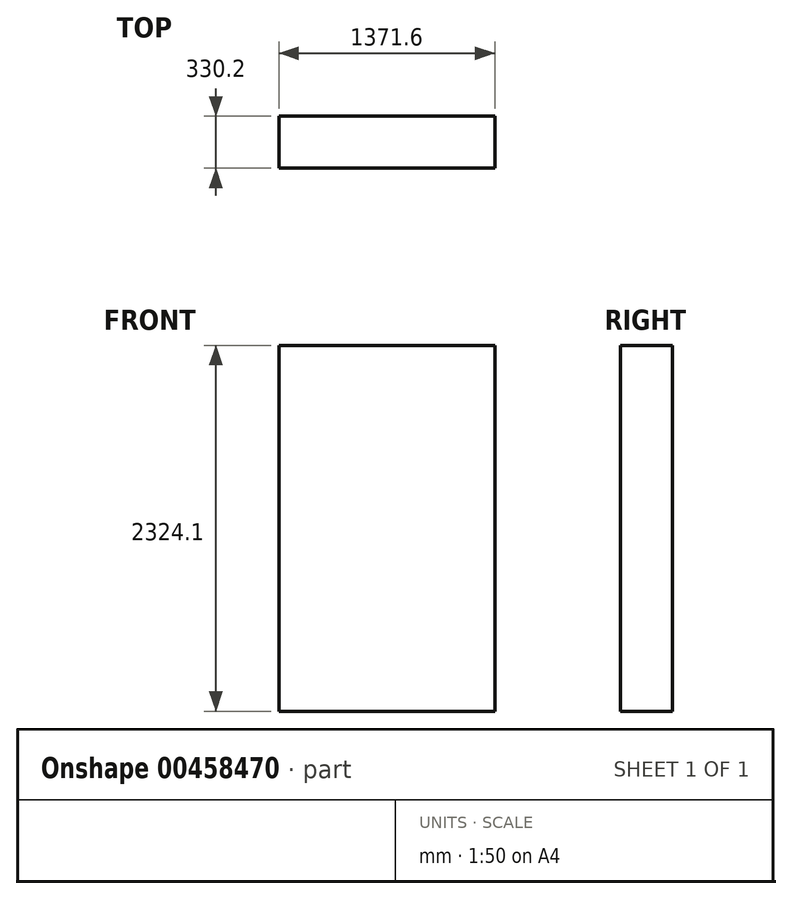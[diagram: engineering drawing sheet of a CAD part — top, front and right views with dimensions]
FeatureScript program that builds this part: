
annotation { "Feature Type Name" : "Feature", "Feature Type Description" : "" }
export const myFeature = defineFeature(function(context is Context, id is Id, definition is map)
    precondition{}
    {
        {
            var Q0;
            Q0=qCreatedBy(makeId("Top.planeOp"),FACE);
            var sketch = newSketch(context, id + "F0", { "sketchPlane" : qUnion([Q0])});
            skLineSegment(sketch, "E0.bottom", {"start": v(-660.33, 158.27) * mm, "end": v(711.27, 158.27) * mm});
            skLineSegment(sketch, "E0.top", {"start": v(-660.33, -171.93) * mm, "end": v(711.27, -171.93) * mm});
            skLineSegment(sketch, "E0.left", {"start": v(-660.33, 158.27) * mm, "end": v(-660.33, -171.93) * mm});
            skLineSegment(sketch, "E0.right", {"start": v(711.27, 158.27) * mm, "end": v(711.27, -171.93) * mm});
            skSolve(sketch);
        }
        {
            var Q0;
            Q0=sQuery(id+"F0.wireOp",EDGE,"E0.bottom");
            var Q1;
            Q1=sQuery(id+"F0.wireOp",EDGE,"E0.left");
            var Q2;
            Q2=sQuery(id+"F0.wireOp",EDGE,"E0.top");
            var Q3;
            Q3=sQuery(id+"F0.wireOp",EDGE,"E0.right");
            extrude(context, id + "F1", {"bodyType" : ToolBodyType.SURFACE, "surfaceEntities" : qUnion([Q0, Q1, Q2, Q3]), "endBound" : BoundingType.SYMMETRIC, "depth" : 2324.1 * mm});
        }
    });
